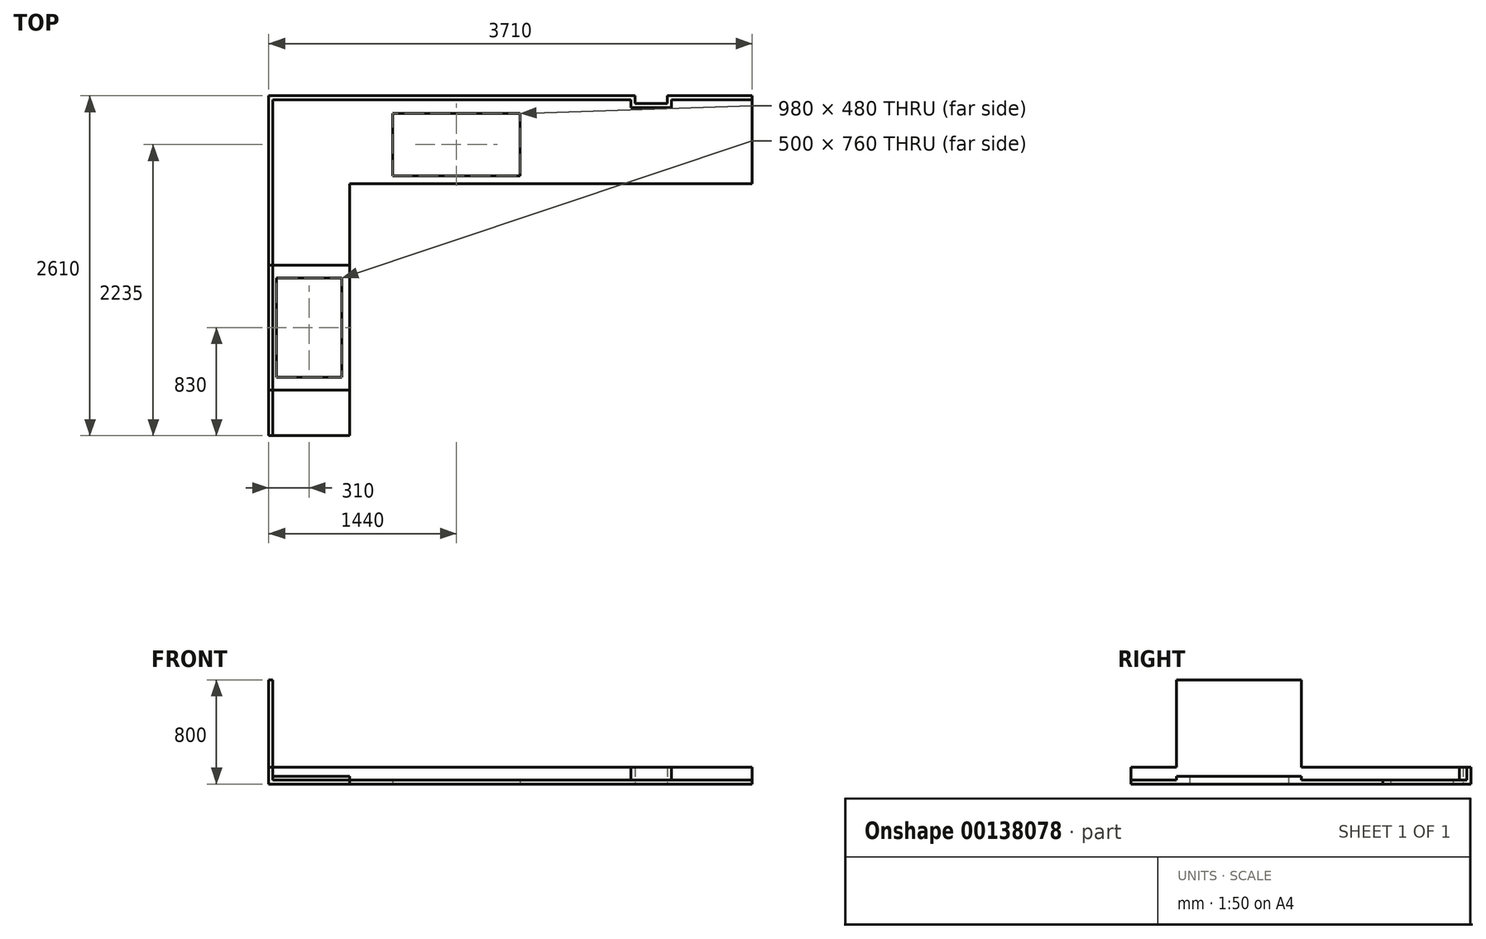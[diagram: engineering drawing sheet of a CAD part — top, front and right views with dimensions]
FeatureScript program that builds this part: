
annotation { "Feature Type Name" : "Feature", "Feature Type Description" : "" }
export const myFeature = defineFeature(function(context is Context, id is Id, definition is map)
    precondition{}
    {
        {
            var Q0;
            Q0=qCreatedBy(makeId("Top.planeOp"),FACE);
            var sketch = newSketch(context, id + "F0", { "sketchPlane" : qUnion([Q0])});
            skLineSegment(sketch, "E0", {"start": v(0, 0) * mm, "end": v(3090, 0) * mm});
            skLineSegment(sketch, "E1", {"start": v(3090, 0) * mm, "end": v(3090, 675) * mm});
            skLineSegment(sketch, "E2", {"start": v(3090, 675) * mm, "end": v(2440, 675) * mm});
            skLineSegment(sketch, "E3", {"start": v(-620, 675) * mm, "end": v(-620, -1935) * mm});
            skLineSegment(sketch, "E4", {"start": v(-620, -1935) * mm, "end": v(0, -1935) * mm});
            skLineSegment(sketch, "E5", {"start": v(0, -1935) * mm, "end": v(0, 0) * mm});
            skLineSegment(sketch, "E6", {"start": v(2440, 675) * mm, "end": v(2440, 615) * mm});
            skLineSegment(sketch, "E7", {"start": v(2440, 615) * mm, "end": v(2190, 615) * mm});
            skLineSegment(sketch, "E8", {"start": v(2190, 615) * mm, "end": v(2190, 675) * mm});
            skLineSegment(sketch, "E9.trimOffspring", {"start": v(2190, 675) * mm, "end": v(-620, 675) * mm});
            skLineSegment(sketch, "E10.bottom", {"start": v(-560, -725) * mm, "end": v(-60, -725) * mm});
            skLineSegment(sketch, "E10.top", {"start": v(-560, -1485) * mm, "end": v(-60, -1485) * mm});
            skLineSegment(sketch, "E10.left", {"start": v(-560, -725) * mm, "end": v(-560, -1485) * mm});
            skLineSegment(sketch, "E10.right", {"start": v(-60, -725) * mm, "end": v(-60, -1485) * mm});
            skLineSegment(sketch, "E11.bottom", {"start": v(330, 540) * mm, "end": v(1310, 540) * mm});
            skLineSegment(sketch, "E11.top", {"start": v(330, 60) * mm, "end": v(1310, 60) * mm});
            skLineSegment(sketch, "E11.left", {"start": v(330, 540) * mm, "end": v(330, 60) * mm});
            skLineSegment(sketch, "E11.right", {"start": v(1310, 540) * mm, "end": v(1310, 60) * mm});
            skSolve(sketch);
        }
        {
            var Q0;
            Q0 = qSketchRegion(id + "F0", true);
            extrude(context, id + "F1", {"entities" : qUnion([Q0]), "depth" : 30 * mm});
        }
        {
            var Q0;
            Q0=makeQuery(id+"F1.opExtrude","CAP_FACE",FACE,{"disambiguationData":[OSD([sQuery(id+"F0.wireOp",EDGE,"E0"),sQuery(id+"F0.wireOp",EDGE,"E1"),sQuery(id+"F0.wireOp",EDGE,"E2"),sQuery(id+"F0.wireOp",EDGE,"E3"),sQuery(id+"F0.wireOp",EDGE,"E4"),sQuery(id+"F0.wireOp",EDGE,"E5"),sQuery(id+"F0.wireOp",EDGE,"E6"),sQuery(id+"F0.wireOp",EDGE,"E7"),sQuery(id+"F0.wireOp",EDGE,"E8"),sQuery(id+"F0.wireOp",EDGE,"E9.trimOffspring"),sQuery(id+"F0.wireOp",EDGE,"E10.bottom"),sQuery(id+"F0.wireOp",EDGE,"E10.top"),sQuery(id+"F0.wireOp",EDGE,"E10.left"),sQuery(id+"F0.wireOp",EDGE,"E10.right"),sQuery(id+"F0.wireOp",EDGE,"E11.bottom"),sQuery(id+"F0.wireOp",EDGE,"E11.top"),sQuery(id+"F0.wireOp",EDGE,"E11.left"),sQuery(id+"F0.wireOp",EDGE,"E11.right")])],"isStart":false});
            var sketch = newSketch(context, id + "F2", { "sketchPlane" : qUnion([Q0])});
            skLineSegment(sketch, "E12.bottom", {"start": v(-620, -625) * mm, "end": v(0, -625) * mm});
            skLineSegment(sketch, "E12.top", {"start": v(-620, -1585) * mm, "end": v(0, -1585) * mm});
            skLineSegment(sketch, "E12.left", {"start": v(-620, -625) * mm, "end": v(-620, -1585) * mm});
            skLineSegment(sketch, "E12.right", {"start": v(0, -625) * mm, "end": v(0, -1585) * mm});
            skLineSegment(sketch, "E13.bottom", {"start": v(-560, -725) * mm, "end": v(-60, -725) * mm});
            skLineSegment(sketch, "E13.top", {"start": v(-560, -1485) * mm, "end": v(-60, -1485) * mm});
            skLineSegment(sketch, "E13.left", {"start": v(-560, -725) * mm, "end": v(-560, -1485) * mm});
            skLineSegment(sketch, "E13.right", {"start": v(-60, -725) * mm, "end": v(-60, -1485) * mm});
            skSolve(sketch);
        }
        {
            var Q0;
            Q0 = qSketchRegion(id + "F2", true);
            extrude(context, id + "F3", {"entities" : qUnion([Q0]), "operationType" : NewBodyOperationType.ADD, "depth" : 30 * mm});
        }
        {
            var Q0;
            Q0=makeQuery(id+"F3.opExtrude","CAP_FACE",FACE,{"disambiguationData":[OSD([sQuery(id+"F2.wireOp",EDGE,"E12.bottom"),sQuery(id+"F2.wireOp",EDGE,"E12.top"),sQuery(id+"F2.wireOp",EDGE,"E12.left"),sQuery(id+"F2.wireOp",EDGE,"E12.right"),sQuery(id+"F2.wireOp",EDGE,"E13.bottom"),sQuery(id+"F2.wireOp",EDGE,"E13.top"),sQuery(id+"F2.wireOp",EDGE,"E13.left"),sQuery(id+"F2.wireOp",EDGE,"E13.right")])],"isStart":false});
            var sketch = newSketch(context, id + "F4", { "sketchPlane" : qUnion([Q0])});
            skLineSegment(sketch, "E14.bottom", {"start": v(-620, -625) * mm, "end": v(-590, -625) * mm});
            skLineSegment(sketch, "E14.top", {"start": v(-620, -1585) * mm, "end": v(-590, -1585) * mm});
            skLineSegment(sketch, "E14.left", {"start": v(-620, -625) * mm, "end": v(-620, -1585) * mm});
            skLineSegment(sketch, "E14.right", {"start": v(-590, -625) * mm, "end": v(-590, -1585) * mm});
            skSolve(sketch);
        }
        {
            var Q0;
            Q0 = qSketchRegion(id + "F4", true);
            extrude(context, id + "F5", {"entities" : qUnion([Q0]), "operationType" : NewBodyOperationType.ADD, "depth" : 740 * mm});
        }
        {
            var Q0;
            {var subQ0=sQuery(id+"F0.wireOp",EDGE,"E9.trimOffspring");var subQ1=sQuery(id+"F0.wireOp",EDGE,"E11.left");var subQ2=sQuery(id+"F0.wireOp",EDGE,"E7");var subQ3=sQuery(id+"F0.wireOp",EDGE,"E11.bottom");var subQ4=sQuery(id+"F0.wireOp",EDGE,"E6");var subQ5=sQuery(id+"F0.wireOp",EDGE,"E5");var subQ6=sQuery(id+"F0.wireOp",EDGE,"E0");var subQ7=sQuery(id+"F0.wireOp",EDGE,"E8");var subQ8=sQuery(id+"F0.wireOp",EDGE,"E11.top");var subQ9=sQuery(id+"F0.wireOp",EDGE,"E1");var subQ10=sQuery(id+"F0.wireOp",EDGE,"E2");var subQ11=sQuery(id+"F0.wireOp",EDGE,"E3");var subQ12=sQuery(id+"F0.wireOp",EDGE,"E11.right");Q0=makeQuery(id+"F3.boolean.opBoolean","SPLIT",FACE,{"disambiguationData":[TD([makeQuery(id+"F1.opExtrude","SWEPT_FACE",FACE,{"disambiguationData":[OSD([subQ6])]})])],"derivedFrom":makeQuery(id+"F1.opExtrude","CAP_FACE",FACE,{"disambiguationData":[OSD([subQ6,subQ9,subQ10,subQ11,sQuery(id+"F0.wireOp",EDGE,"E4"),subQ5,subQ4,subQ2,subQ7,subQ0,sQuery(id+"F0.wireOp",EDGE,"E10.bottom"),sQuery(id+"F0.wireOp",EDGE,"E10.top"),sQuery(id+"F0.wireOp",EDGE,"E10.left"),sQuery(id+"F0.wireOp",EDGE,"E10.right"),subQ3,subQ8,subQ1,subQ12])],"isStart":false})});}
            var sketch = newSketch(context, id + "F6", { "sketchPlane" : qUnion([Q0])});
            skLineSegment(sketch, "E15.bottom", {"start": v(3090, 675) * mm, "end": v(2440, 675) * mm});
            skLineSegment(sketch, "E15.top", {"start": v(3090, 645) * mm, "end": v(2440, 645) * mm});
            skLineSegment(sketch, "E15.left", {"start": v(3090, 675) * mm, "end": v(3090, 645) * mm});
            skLineSegment(sketch, "E15.right", {"start": v(2440, 675) * mm, "end": v(2440, 645) * mm});
            skLineSegment(sketch, "E16.bottom", {"start": v(2190, 675) * mm, "end": v(-620, 675) * mm});
            skLineSegment(sketch, "E16.top", {"start": v(2190, 645) * mm, "end": v(-620, 645) * mm});
            skLineSegment(sketch, "E16.left", {"start": v(2190, 675) * mm, "end": v(2190, 645) * mm});
            skLineSegment(sketch, "E16.right", {"start": v(-620, 675) * mm, "end": v(-620, 645) * mm});
            skLineSegment(sketch, "E17.bottom", {"start": v(-620, 645) * mm, "end": v(-590, 645) * mm});
            skLineSegment(sketch, "E17.top", {"start": v(-620, -625) * mm, "end": v(-590, -625) * mm});
            skLineSegment(sketch, "E17.left", {"start": v(-620, 645) * mm, "end": v(-620, -625) * mm});
            skLineSegment(sketch, "E17.right", {"start": v(-590, 645) * mm, "end": v(-590, -625) * mm});
            skLineSegment(sketch, "E18.bottom", {"start": v(2160, 615) * mm, "end": v(2470, 615) * mm});
            skLineSegment(sketch, "E18.top", {"start": v(2160, 585) * mm, "end": v(2470, 585) * mm});
            skLineSegment(sketch, "E18.left", {"start": v(2160, 615) * mm, "end": v(2160, 585) * mm});
            skLineSegment(sketch, "E18.right", {"start": v(2470, 615) * mm, "end": v(2470, 585) * mm});
            skLineSegment(sketch, "E19.bottom", {"start": v(2470, 615) * mm, "end": v(2440, 615) * mm});
            skLineSegment(sketch, "E19.top", {"start": v(2470, 645) * mm, "end": v(2440, 645) * mm});
            skLineSegment(sketch, "E19.left", {"start": v(2470, 615) * mm, "end": v(2470, 645) * mm});
            skLineSegment(sketch, "E19.right", {"start": v(2440, 615) * mm, "end": v(2440, 645) * mm});
            skLineSegment(sketch, "E20.bottom", {"start": v(2160, 615) * mm, "end": v(2190, 615) * mm});
            skLineSegment(sketch, "E20.top", {"start": v(2160, 645) * mm, "end": v(2190, 645) * mm});
            skLineSegment(sketch, "E20.left", {"start": v(2160, 615) * mm, "end": v(2160, 645) * mm});
            skLineSegment(sketch, "E20.right", {"start": v(2190, 615) * mm, "end": v(2190, 645) * mm});
            skSolve(sketch);
        }
        {
            var Q0;
            Q0 = qSketchRegion(id + "F6", true);
            extrude(context, id + "F7", {"entities" : qUnion([Q0]), "operationType" : NewBodyOperationType.ADD, "depth" : 100 * mm});
        }
        {
            var Q0;
            {var subQ0=sQuery(id+"F0.wireOp",EDGE,"E5");var subQ1=sQuery(id+"F0.wireOp",EDGE,"E4");var subQ2=sQuery(id+"F0.wireOp",EDGE,"E3");Q0=makeQuery(id+"F3.boolean.opBoolean","SPLIT",FACE,{"disambiguationData":[TD([makeQuery(id+"F1.opExtrude","SWEPT_FACE",FACE,{"disambiguationData":[OSD([subQ1])]})])],"derivedFrom":makeQuery(id+"F1.opExtrude","CAP_FACE",FACE,{"disambiguationData":[OSD([sQuery(id+"F0.wireOp",EDGE,"E0"),sQuery(id+"F0.wireOp",EDGE,"E1"),sQuery(id+"F0.wireOp",EDGE,"E2"),subQ2,subQ1,subQ0,sQuery(id+"F0.wireOp",EDGE,"E6"),sQuery(id+"F0.wireOp",EDGE,"E7"),sQuery(id+"F0.wireOp",EDGE,"E8"),sQuery(id+"F0.wireOp",EDGE,"E9.trimOffspring"),sQuery(id+"F0.wireOp",EDGE,"E10.bottom"),sQuery(id+"F0.wireOp",EDGE,"E10.top"),sQuery(id+"F0.wireOp",EDGE,"E10.left"),sQuery(id+"F0.wireOp",EDGE,"E10.right"),sQuery(id+"F0.wireOp",EDGE,"E11.bottom"),sQuery(id+"F0.wireOp",EDGE,"E11.top"),sQuery(id+"F0.wireOp",EDGE,"E11.left"),sQuery(id+"F0.wireOp",EDGE,"E11.right")])],"isStart":false})});}
            var sketch = newSketch(context, id + "F8", { "sketchPlane" : qUnion([Q0])});
            skLineSegment(sketch, "E21.bottom", {"start": v(-620, -1935) * mm, "end": v(-590, -1935) * mm});
            skLineSegment(sketch, "E21.top", {"start": v(-620, -1585) * mm, "end": v(-590, -1585) * mm});
            skLineSegment(sketch, "E21.left", {"start": v(-620, -1935) * mm, "end": v(-620, -1585) * mm});
            skLineSegment(sketch, "E21.right", {"start": v(-590, -1935) * mm, "end": v(-590, -1585) * mm});
            skSolve(sketch);
        }
        {
            var Q0;
            Q0 = qSketchRegion(id + "F8", true);
            extrude(context, id + "F9", {"entities" : qUnion([Q0]), "operationType" : NewBodyOperationType.ADD, "depth" : 100 * mm});
        }
    });
